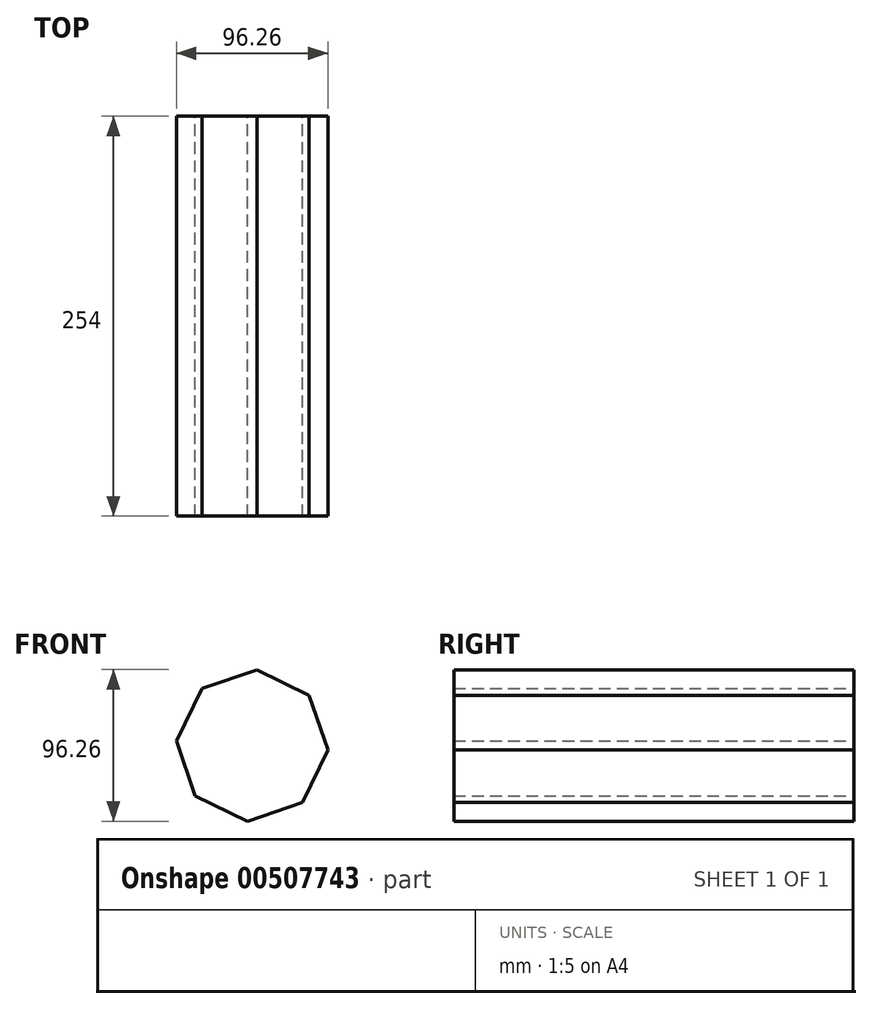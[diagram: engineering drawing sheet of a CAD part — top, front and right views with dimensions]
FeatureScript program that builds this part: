
annotation { "Feature Type Name" : "Feature", "Feature Type Description" : "" }
export const myFeature = defineFeature(function(context is Context, id is Id, definition is map)
    precondition{}
    {
        {
            var Q0;
            Q0=qCreatedBy(makeId("Front.planeOp"),FACE);
            var sketch = newSketch(context, id + "F0", { "sketchPlane" : qUnion([Q0])});
            skCircle(sketch, "E0.cCircle", {"center": v(0, 0) * mm, "radius": 48.22 * mm, "construction": true});
            skLineSegment(sketch, "E0.0", {"start": v(36.14, 31.92) * mm, "end": v(48.13, -2.99) * mm});
            skLineSegment(sketch, "E0.1", {"start": v(48.13, -2.99) * mm, "end": v(31.92, -36.14) * mm});
            skLineSegment(sketch, "E0.2", {"start": v(31.92, -36.14) * mm, "end": v(-2.99, -48.13) * mm});
            skLineSegment(sketch, "E0.3", {"start": v(-2.99, -48.13) * mm, "end": v(-36.14, -31.92) * mm});
            skLineSegment(sketch, "E0.4", {"start": v(-36.14, -31.92) * mm, "end": v(-48.13, 2.99) * mm});
            skLineSegment(sketch, "E0.5", {"start": v(-48.13, 2.99) * mm, "end": v(-31.92, 36.14) * mm});
            skLineSegment(sketch, "E0.6", {"start": v(-31.92, 36.14) * mm, "end": v(2.99, 48.13) * mm});
            skLineSegment(sketch, "E0.7", {"start": v(2.99, 48.13) * mm, "end": v(36.14, 31.92) * mm});
            skSolve(sketch);
        }
        {
            var Q0;
            Q0=makeQuery(id+"F0.imprint","IMPRINT",FACE,{"disambiguationData":[TD([[makeQuery(id+"F0.imprint","IMPRINT",EDGE,{"derivedFrom":sQuery(id+"F0.wireOp",EDGE,"E0.0")}),-1.0]])]});
            extrude(context, id + "F1", {"entities" : qUnion([Q0]), "depth" : 254 * mm});
        }
    });
